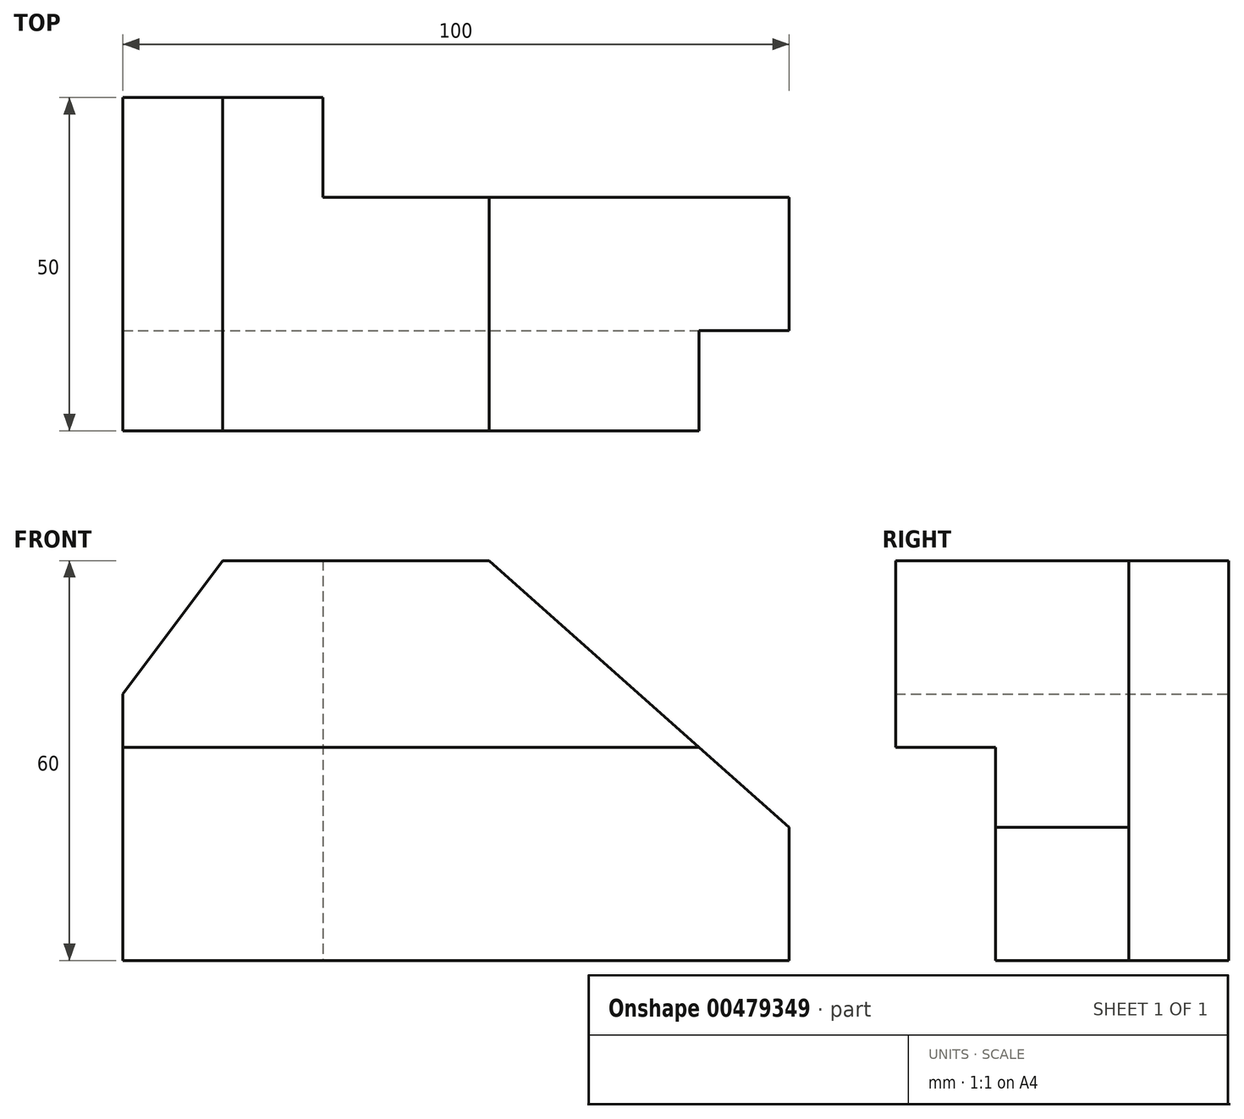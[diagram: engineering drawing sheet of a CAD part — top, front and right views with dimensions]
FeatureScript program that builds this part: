
annotation { "Feature Type Name" : "Feature", "Feature Type Description" : "" }
export const myFeature = defineFeature(function(context is Context, id is Id, definition is map)
    precondition{}
    {
        {
            var Q0;
            Q0=qCreatedBy(makeId("Top.planeOp"),FACE);
            var sketch = newSketch(context, id + "F0", { "sketchPlane" : qUnion([Q0])});
            skLineSegment(sketch, "E0.bottom", {"start": v(0, 0) * mm, "end": v(100, 0) * mm});
            skLineSegment(sketch, "E0.top", {"start": v(0, 50) * mm, "end": v(100, 50) * mm});
            skLineSegment(sketch, "E0.left", {"start": v(0, 0) * mm, "end": v(0, 50) * mm});
            skLineSegment(sketch, "E0.right", {"start": v(100, 0) * mm, "end": v(100, 50) * mm});
            skSolve(sketch);
        }
        {
            var Q0;
            Q0 = qSketchRegion(id + "F0", true);
            extrude(context, id + "F1", {"entities" : qUnion([Q0]), "depth" : 60 * mm});
        }
        {
            var Q0;
            Q0=makeQuery(id+"F1.opExtrude","SWEPT_FACE",FACE,{"disambiguationData":[OSD([sQuery(id+"F0.wireOp",EDGE,"E0.right")])]});
            var sketch = newSketch(context, id + "F2", { "sketchPlane" : qUnion([Q0])});
            skLineSegment(sketch, "E1.bottom", {"start": v(0, 0) * mm, "end": v(15, 0) * mm});
            skLineSegment(sketch, "E1.top", {"start": v(0, 32) * mm, "end": v(15, 32) * mm});
            skLineSegment(sketch, "E1.left", {"start": v(0, 0) * mm, "end": v(0, 32) * mm});
            skLineSegment(sketch, "E1.right", {"start": v(15, 0) * mm, "end": v(15, 32) * mm});
            skSolve(sketch);
        }
        {
            var Q0;
            Q0=makeQuery(id+"F2.imprint","IMPRINT",FACE,{"disambiguationData":[TD([[makeQuery(id+"F2.imprint","IMPRINT",EDGE,{"derivedFrom":sQuery(id+"F2.wireOp",EDGE,"E1.bottom")}),1.0]])]});
            extrude(context, id + "F3", {"entities" : qUnion([Q0]), "operationType" : NewBodyOperationType.REMOVE, "endBound" : BoundingType.THROUGH_ALL, "oppositeDirection" : true, "depth" : 25 * mm});
        }
        {
            var Q0;
            Q0=makeQuery(id+"F1.opExtrude","SWEPT_FACE",FACE,{"disambiguationData":[OSD([sQuery(id+"F0.wireOp",EDGE,"E0.top")])]});
            var sketch = newSketch(context, id + "F4", { "sketchPlane" : qUnion([Q0])});
            skLineSegment(sketch, "E2", {"start": v(-55, 60) * mm, "end": v(-100, 20) * mm});
            skLineSegment(sketch, "E3", {"start": v(-15, 60) * mm, "end": v(0, 40) * mm});
            skSolve(sketch);
        }
        {
            var Q0;
            {var subQ0=sQuery(id+"F4.wireOp",EDGE,"E3");Q0=makeQuery(id+"F4.imprint","IMPRINT",FACE,{"disambiguationData":[TD([[makeQuery(id+"F4.imprint","IMPRINT",EDGE,{"derivedFrom":subQ0}),1.0]])]});}
            var Q1;
            {var subQ0=sQuery(id+"F4.wireOp",EDGE,"E2");Q1=makeQuery(id+"F4.imprint","IMPRINT",FACE,{"disambiguationData":[TD([[makeQuery(id+"F4.imprint","IMPRINT",EDGE,{"derivedFrom":subQ0}),-1.0]])]});}
            extrude(context, id + "F5", {"entities" : qUnion([Q0, Q1]), "operationType" : NewBodyOperationType.REMOVE, "endBound" : BoundingType.THROUGH_ALL, "oppositeDirection" : true, "depth" : 25 * mm});
        }
        {
            var Q0;
            Q0=makeQuery(id+"F1.opExtrude","CAP_FACE",FACE,{"disambiguationData":[OSD([sQuery(id+"F0.wireOp",EDGE,"E0.bottom"),sQuery(id+"F0.wireOp",EDGE,"E0.top"),sQuery(id+"F0.wireOp",EDGE,"E0.left"),sQuery(id+"F0.wireOp",EDGE,"E0.right")])],"isStart":true});
            var sketch = newSketch(context, id + "F6", { "sketchPlane" : qUnion([Q0])});
            skLineSegment(sketch, "E4.bottom", {"start": v(100, -50) * mm, "end": v(30, -50) * mm});
            skLineSegment(sketch, "E4.top", {"start": v(100, -35) * mm, "end": v(30, -35) * mm});
            skLineSegment(sketch, "E4.left", {"start": v(100, -50) * mm, "end": v(100, -35) * mm});
            skLineSegment(sketch, "E4.right", {"start": v(30, -50) * mm, "end": v(30, -35) * mm});
            skSolve(sketch);
        }
        {
            var Q0;
            Q0 = qSketchRegion(id + "F6", true);
            extrude(context, id + "F7", {"entities" : qUnion([Q0]), "operationType" : NewBodyOperationType.REMOVE, "endBound" : BoundingType.THROUGH_ALL, "oppositeDirection" : true, "depth" : 25 * mm});
        }
    });
